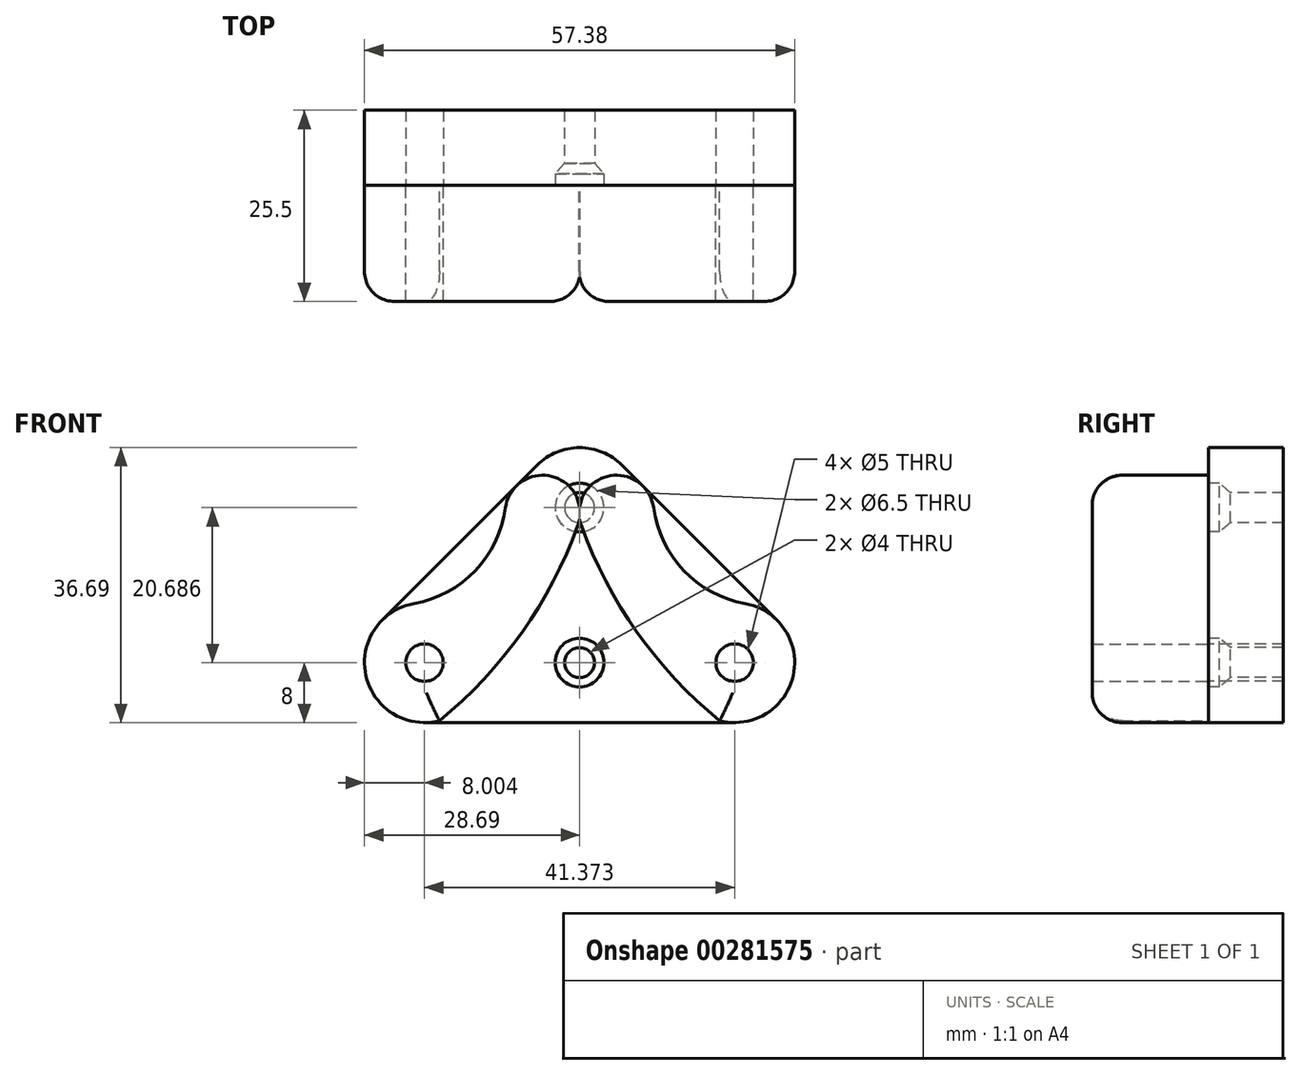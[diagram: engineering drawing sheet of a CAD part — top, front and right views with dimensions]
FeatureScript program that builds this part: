
annotation { "Feature Type Name" : "Feature", "Feature Type Description" : "" }
export const myFeature = defineFeature(function(context is Context, id is Id, definition is map)
    precondition{}
    {
        {
            var Q0;
            Q0=qCreatedBy(makeId("Front.planeOp"),FACE);
            var sketch = newSketch(context, id + "F0", { "sketchPlane" : qUnion([Q0])});
            skLineSegment(sketch, "E0", {"start": v(0, 20) * mm, "end": v(-40, -20) * mm});
            skLineSegment(sketch, "E1", {"start": v(-40, -20) * mm, "end": v(40, -20) * mm});
            skLineSegment(sketch, "E2", {"start": v(40, -20) * mm, "end": v(0, 20) * mm});
            skLineSegment(sketch, "E3", {"start": v(20, 0) * mm, "end": v(0, 0) * mm, "construction": true});
            skLineSegment(sketch, "E4", {"start": v(0, 0) * mm, "end": v(-20, 0) * mm, "construction": true});
            skLineSegment(sketch, "E5", {"start": v(0, 0) * mm, "end": v(0, -20) * mm, "construction": true});
            skSolve(sketch);
        }
        {
            var Q0;
            Q0 = qSketchRegion(id + "F0", true);
            extrude(context, id + "F1", {"entities" : qUnion([Q0]), "endBound" : BoundingType.SYMMETRIC, "depth" : 10 * mm});
        }
        {
            var Q0;
            Q0=makeQuery(id+"F1.opExtrude","SWEPT_EDGE",EDGE,{"disambiguationData":[OSD([sQuery(id+"F0.wireOp",EDGE,"E0"),sQuery(id+"F0.wireOp",EDGE,"E2")])]});
            var Q1;
            Q1=makeQuery(id+"F1.opExtrude","SWEPT_EDGE",EDGE,{"disambiguationData":[OSD([sQuery(id+"F0.wireOp",EDGE,"E1"),sQuery(id+"F0.wireOp",EDGE,"E2")])]});
            var Q2;
            Q2=makeQuery(id+"F1.opExtrude","SWEPT_EDGE",EDGE,{"disambiguationData":[OSD([sQuery(id+"F0.wireOp",EDGE,"E0"),sQuery(id+"F0.wireOp",EDGE,"E1")])]});
            fillet(context, id + "F2", {"entities" : qUnion([Q0, Q1, Q2]), "radius" : 8 * mm, "tangentPropagation" : true, "allowEdgeOverflow" : false});
        }
        {
            var Q0;
            Q0=makeQuery(id+"F1.opExtrude","CAP_FACE",FACE,{"disambiguationData":[OSD([sQuery(id+"F0.wireOp",EDGE,"E0"),sQuery(id+"F0.wireOp",EDGE,"E1"),sQuery(id+"F0.wireOp",EDGE,"E2")])],"isStart":false});
            var sketch = newSketch(context, id + "F3", { "sketchPlane" : qUnion([Q0])});
            skArc(sketch, "E6", {"start": v(-22.1, -4.13) * mm, "mid": v(-28.5, -13.7) * mm, "end": v(-18.69, -19.75) * mm});
            skCircle(sketch, "E7", {"center": v(-20.69, -12) * mm, "radius": 2.5 * mm});
            skArc(sketch, "E8", {"start": v(-0.23, 6.3) * mm, "mid": v(-3.74, 12.86) * mm, "end": v(-9.89, 8.66) * mm});
            skArc(sketch, "E9", {"start": v(-22.1, -4.13) * mm, "mid": v(-13.9, 0.28) * mm, "end": v(-9.89, 8.66) * mm});
            skArc(sketch, "E10", {"start": v(-18.69, -19.75) * mm, "mid": v(-7.7, -7.97) * mm, "end": v(-0.23, 6.3) * mm});
            skSolve(sketch);
        }
        {
            var Q0;
            Q0 = qSketchRegion(id + "F3", true);
            extrude(context, id + "F4", {"entities" : qUnion([Q0]), "depth" : 20 * mm - 4.5 * mm});
        }
        {
            var Q0;
            Q0=makeQuery(id+"F1.opExtrude","CAP_FACE",FACE,{"disambiguationData":[OSD([sQuery(id+"F0.wireOp",EDGE,"E0"),sQuery(id+"F0.wireOp",EDGE,"E1"),sQuery(id+"F0.wireOp",EDGE,"E2")])],"isStart":false});
            var sketch = newSketch(context, id + "F5", { "sketchPlane" : qUnion([Q0])});
            skCircle(sketch, "E11.0", {"center": v(-20.69, -12) * mm, "radius": 2.5 * mm});
            skCircle(sketch, "E12", {"center": v(20.69, -12) * mm, "radius": 2.5 * mm});
            skSolve(sketch);
        }
        {
            var Q0;
            Q0 = qSketchRegion(id + "F5", true);
            extrude(context, id + "F6", {"entities" : qUnion([Q0]), "operationType" : NewBodyOperationType.REMOVE, "endBound" : BoundingType.THROUGH_ALL, "oppositeDirection" : true, "depth" : 25 * mm});
        }
        {
            var Q0;
            Q0=makeQuery(id+"F4.opExtrude","SWEPT_BODY",BODY,{"disambiguationData":[OSD([sQuery(id+"F3.wireOp",EDGE,"E6"),sQuery(id+"F3.wireOp",EDGE,"E7"),sQuery(id+"F3.wireOp",EDGE,"E8"),sQuery(id+"F3.wireOp",EDGE,"E9"),sQuery(id+"F3.wireOp",EDGE,"E10")])]});
            var Q1;
            Q1=qCreatedBy(makeId("Right.planeOp"),FACE);
            mirror(context, id + "F7", {"entities" : qUnion([Q0]), "mirrorPlane" : qUnion([Q1])});
        }
        {
            var Q0;
            Q0=makeQuery(id+"F4.opExtrude","CAP_EDGE",EDGE,{"disambiguationData":[OSD([sQuery(id+"F3.wireOp",EDGE,"E10")])],"isStart":false});
            var Q1;
            Q1=makeQuery(id+"F7.opPattern","COPY",EDGE,{"derivedFrom":makeQuery(id+"F4.opExtrude","CAP_EDGE",EDGE,{"disambiguationData":[OSD([sQuery(id+"F3.wireOp",EDGE,"E10")])],"isStart":false}),"instanceName":"1"});
            fillet(context, id + "F8", {"entities" : qUnion([Q0, Q1]), "radius" : 4 * mm, "tangentPropagation" : true, "allowEdgeOverflow" : false});
        }
        {
            var Q0;
            Q0=makeQuery(id+"F1.opExtrude","CAP_FACE",FACE,{"disambiguationData":[OSD([sQuery(id+"F0.wireOp",EDGE,"E0"),sQuery(id+"F0.wireOp",EDGE,"E1"),sQuery(id+"F0.wireOp",EDGE,"E2")])],"isStart":false});
            var sketch = newSketch(context, id + "F9", { "sketchPlane" : qUnion([Q0])});
            skPoint(sketch, "E13", {"position": v(0, 8.69) * mm});
            skPoint(sketch, "E14", {"position": v(0, -12) * mm});
            skLineSegment(sketch, "E15", {"start": v(-20.69, -12) * mm, "end": v(20.69, -12) * mm, "construction": true});
            skSolve(sketch);
        }
        {
            var Q0;
            {var subQ0=sQuery(id+"F0.wireOp",EDGE,"E0");Q0=makeQuery(id+"F9.imprint","IMPRINT",FACE,{"disambiguationData":[TD([[makeQuery(id+"F9.imprint","IMPRINT",EDGE,{"derivedFrom":makeQuery(id+"F1.opExtrude","CAP_EDGE",EDGE,{"disambiguationData":[OSD([subQ0])],"isStart":false})}),1.0]])]});}
            var sketch = newSketch(context, id + "F10", { "sketchPlane" : qUnion([Q0])});
            skCircle(sketch, "E16", {"center": v(0, 8.69) * mm, "radius": 3.25 * mm});
            skCircle(sketch, "E17", {"center": v(0, -12) * mm, "radius": 3.25 * mm});
            skSolve(sketch);
        }
        {
            var Q0;
            Q0 = qSketchRegion(id + "F10", true);
            extrude(context, id + "F11", {"entities" : qUnion([Q0]), "operationType" : NewBodyOperationType.REMOVE, "oppositeDirection" : true, "depth" : 1.5 * mm});
        }
        {
            var Q0;
            Q0=makeQuery(id+"F11.boolean.opBoolean","COPY",FACE,{"derivedFrom":makeQuery(id+"F11.opExtrude","CAP_FACE",FACE,{"disambiguationData":[OSD([sQuery(id+"F10.wireOp",EDGE,"E16")])],"isStart":false})});
            var sketch = newSketch(context, id + "F12", { "sketchPlane" : qUnion([Q0])});
            skPoint(sketch, "E18", {"position": v(0, 8.69) * mm});
            skPoint(sketch, "E19", {"position": v(0, -12) * mm});
            skSolve(sketch);
        }
        {
            var Q0;
            Q0=sQuery(id+"F12.wireOp",VERTEX,"E18");
            var Q1;
            Q1=sQuery(id+"F12.wireOp",VERTEX,"E19");
            var Q2;
            Q2=makeQuery(id+"F1.opExtrude","SWEPT_BODY",BODY,{"disambiguationData":[OSD([sQuery(id+"F0.wireOp",EDGE,"E0"),sQuery(id+"F0.wireOp",EDGE,"E1"),sQuery(id+"F0.wireOp",EDGE,"E2")])]});
            hole(context, id + "F13", {"style" : HoleStyle.C_SINK, "endStyle" : HoleEndStyle.THROUGH, "holeDiameter" : 4 * mm, "cSinkDiameter" : 6.5 * mm, "cSinkAngle" : 82 * degree, "tappedDepth" : 12 * mm, "tapClearance" : 3, "startFromSketch" : true, "locations" : qUnion([Q0, Q1]), "scope" : qUnion([Q2])});
        }
    });
